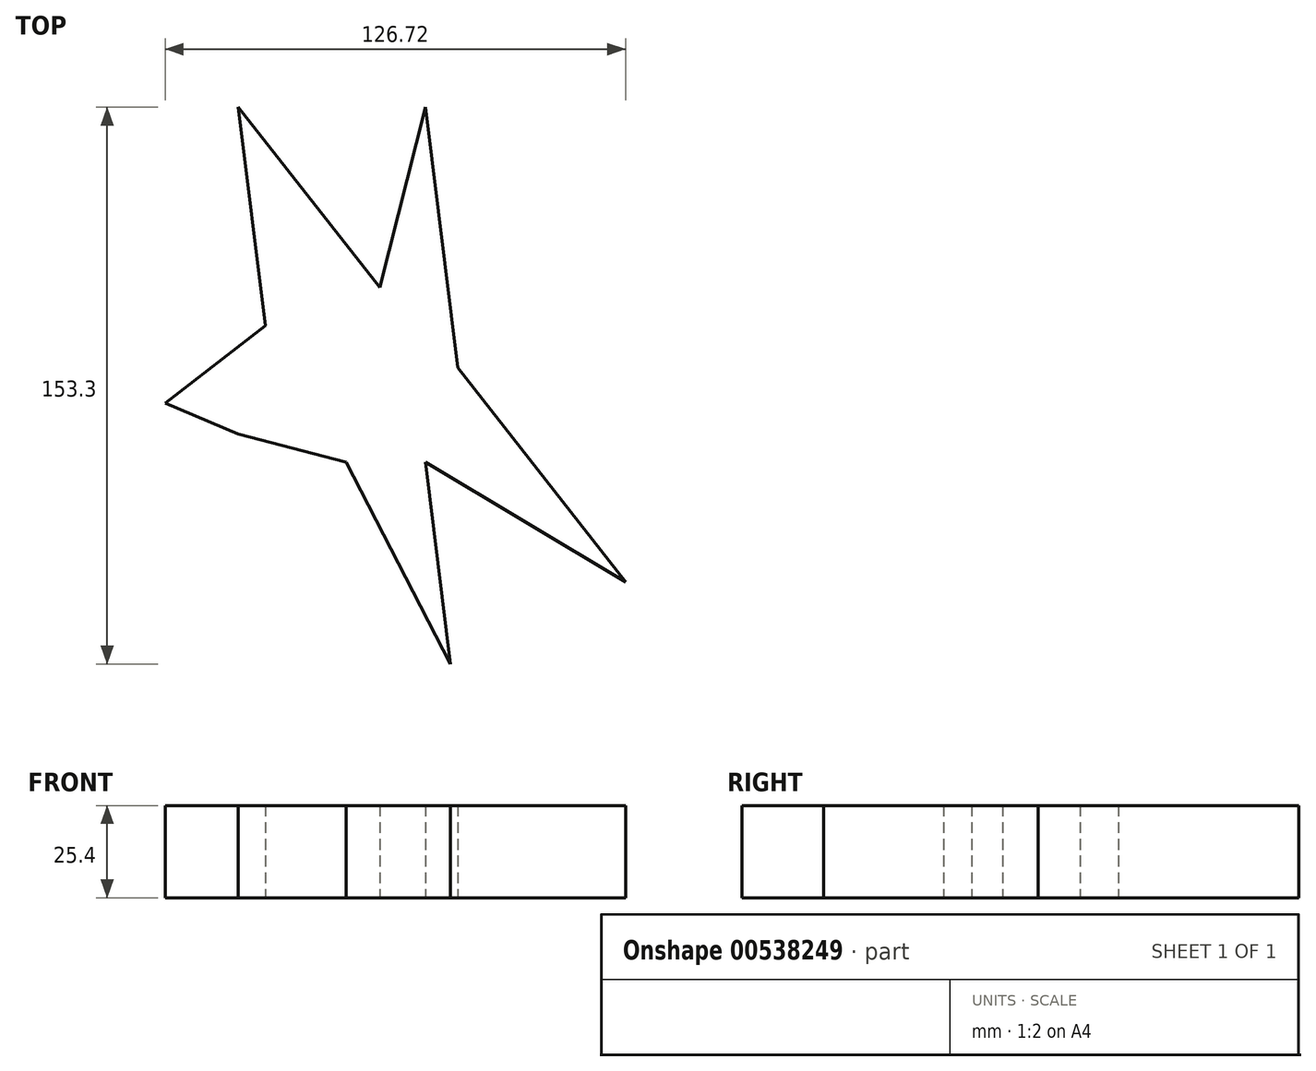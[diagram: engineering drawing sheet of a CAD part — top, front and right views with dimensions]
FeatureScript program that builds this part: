
annotation { "Feature Type Name" : "Feature", "Feature Type Description" : "" }
export const myFeature = defineFeature(function(context is Context, id is Id, definition is map)
    precondition{}
    {
        {
            var Q0;
            Q0=qCreatedBy(makeId("Top.planeOp"),FACE);
            var sketch = newSketch(context, id + "F0", { "sketchPlane" : qUnion([Q0])});
            skLineSegment(sketch, "E0", {"start": v(-189.35, -143.19) * mm, "end": v(-196.78, -83.02) * mm});
            skLineSegment(sketch, "E1", {"start": v(-196.78, -83.02) * mm, "end": v(-157.77, -132.6) * mm});
            skLineSegment(sketch, "E2", {"start": v(-157.77, -132.6) * mm, "end": v(-145.24, -83.02) * mm});
            skLineSegment(sketch, "E3", {"start": v(-145.24, -83.02) * mm, "end": v(-136.39, -154.76) * mm});
            skLineSegment(sketch, "E4", {"start": v(-136.39, -154.76) * mm, "end": v(-90.17, -213.74) * mm});
            skLineSegment(sketch, "E5", {"start": v(-90.17, -213.74) * mm, "end": v(-145.24, -180.78) * mm});
            skLineSegment(sketch, "E6", {"start": v(-145.24, -180.78) * mm, "end": v(-138.39, -236.32) * mm});
            skLineSegment(sketch, "E7", {"start": v(-138.39, -236.32) * mm, "end": v(-167.12, -180.78) * mm});
            skLineSegment(sketch, "E8", {"start": v(-167.12, -180.78) * mm, "end": v(-196.78, -173.02) * mm});
            skLineSegment(sketch, "E9", {"start": v(-196.78, -173.02) * mm, "end": v(-216.9, -164.55) * mm});
            skLineSegment(sketch, "E10", {"start": v(-216.9, -164.55) * mm, "end": v(-189.35, -143.19) * mm});
            skSolve(sketch);
        }
        {
            var Q0;
            Q0 = qSketchRegion(id + "F0", true);
            extrude(context, id + "F1", {"entities" : qUnion([Q0]), "depth" : 25.4 * mm, "offsetDistance" : 25.4 * mm});
        }
    });
